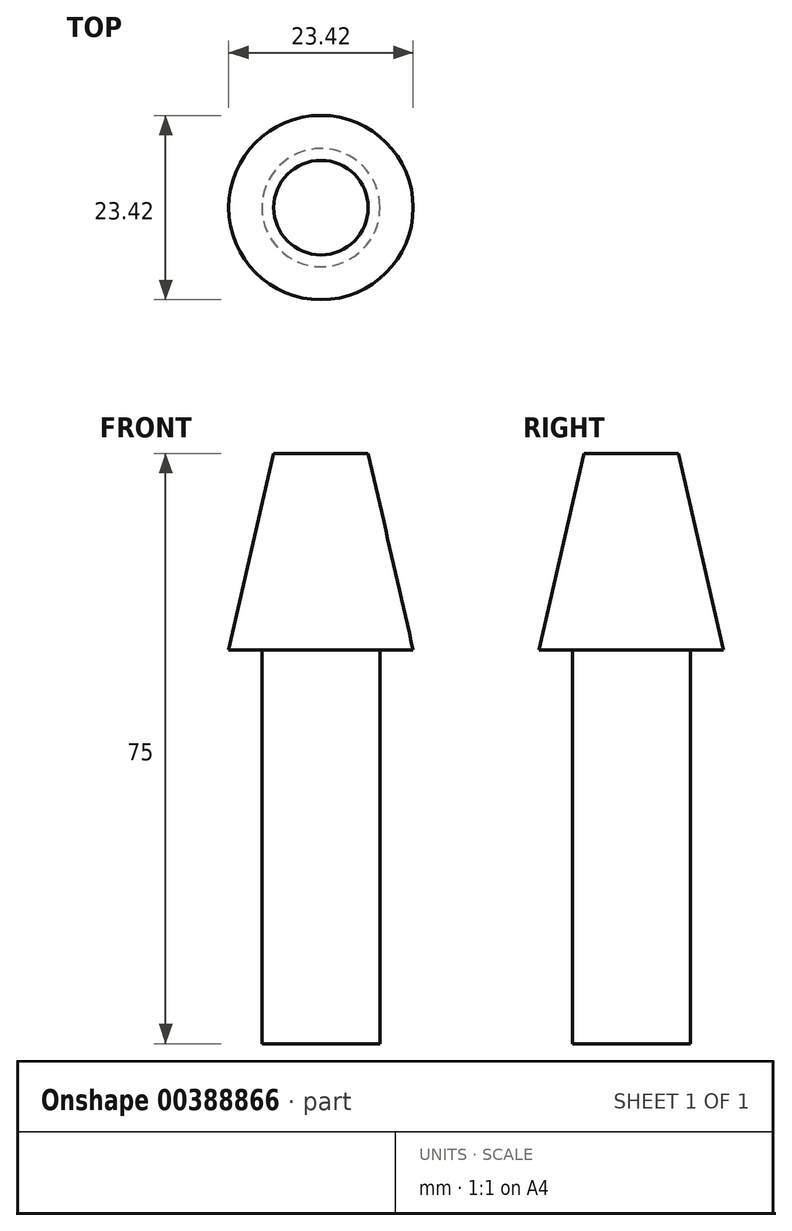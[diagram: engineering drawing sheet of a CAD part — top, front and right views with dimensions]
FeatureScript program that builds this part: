
annotation { "Feature Type Name" : "Feature", "Feature Type Description" : "" }
export const myFeature = defineFeature(function(context is Context, id is Id, definition is map)
    precondition{}
    {
        {
            var Q0;
            Q0=qCreatedBy(makeId("Top.planeOp"),FACE);
            var sketch = newSketch(context, id + "F0", { "sketchPlane" : qUnion([Q0])});
            skCircle(sketch, "E0", {"center": v(0, 0) * mm, "radius": 14 * mm});
            skSolve(sketch);
        }
        {
            var Q0;
            Q0 = qSketchRegion(id + "F0", true);
            extrude(context, id + "F1", {"entities" : qUnion([Q0]), "depth" : 25 * mm, "offsetDistance" : 25 * mm});
        }
        {
            var Q0;
            Q0=makeQuery(id+"F1.opExtrude","CAP_EDGE",EDGE,{"disambiguationData":[OSD([sQuery(id+"F0.wireOp",EDGE,"E0")])],"isStart":false});
            chamfer(context, id + "F2", {"entities" : qUnion([Q0]), "chamferType" : ChamferType.TWO_OFFSETS, "width1" : 8 * mm, "oppositeDirection" : false, "width2" : 35 * mm, "tangentPropagation" : true});
        }
        {
            var Q0;
            Q0=makeQuery(id+"F1.opExtrude","CAP_FACE",FACE,{"disambiguationData":[OSD([sQuery(id+"F0.wireOp",EDGE,"E0")])],"isStart":true});
            var sketch = newSketch(context, id + "F3", { "sketchPlane" : qUnion([Q0])});
            skCircle(sketch, "E1", {"center": v(0, 0) * mm, "radius": 7.5 * mm});
            skSolve(sketch);
        }
        {
            var Q0;
            Q0 = qSketchRegion(id + "F3", true);
            extrude(context, id + "F4", {"entities" : qUnion([Q0]), "operationType" : NewBodyOperationType.ADD, "depth" : 50 * mm, "offsetDistance" : 25 * mm});
        }
    });
